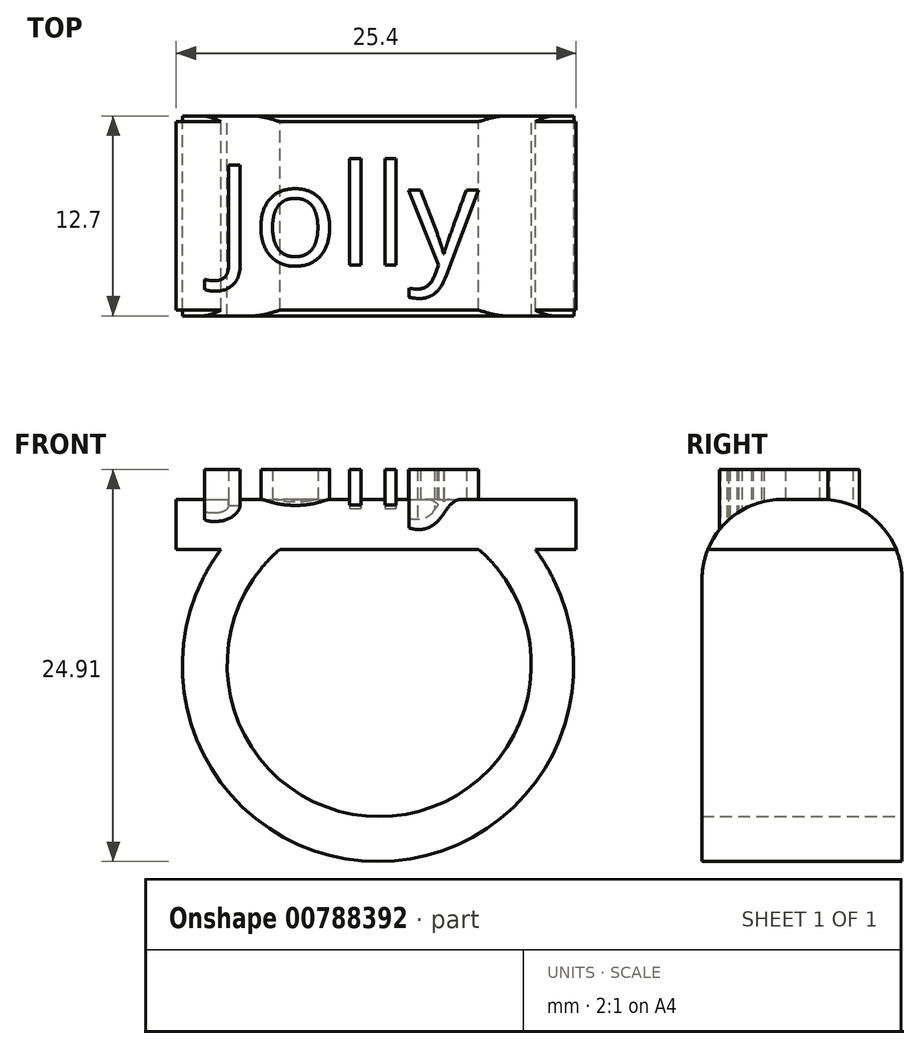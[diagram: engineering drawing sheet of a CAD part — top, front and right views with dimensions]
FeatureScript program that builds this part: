
annotation { "Feature Type Name" : "Feature", "Feature Type Description" : "" }
export const myFeature = defineFeature(function(context is Context, id is Id, definition is map)
    precondition{}
    {
        {
            var Q0;
            Q0=qCreatedBy(makeId("Top.planeOp"),FACE);
            var sketch = newSketch(context, id + "F0", { "sketchPlane" : qUnion([Q0])});
            skLineSegment(sketch, "E0.bottom", {"start": v(-13.4, 0) * mm, "end": v(12, 0) * mm});
            skLineSegment(sketch, "E0.top", {"start": v(-13.4, -12.7) * mm, "end": v(12, -12.7) * mm});
            skLineSegment(sketch, "E0.left", {"start": v(-13.4, 0) * mm, "end": v(-13.4, -12.7) * mm});
            skLineSegment(sketch, "E0.right", {"start": v(12, 0) * mm, "end": v(12, -12.7) * mm});
            skSolve(sketch);
        }
        {
            var Q0;
            Q0=qSketchRegion(id+"F0",true);
            extrude(context, id + "F1", {"entities" : qUnion([Q0]), "depth" : 3.17 * mm, "offsetDistance" : 25.4 * mm});
        }
        {
            var Q0;
            Q0=qCreatedBy(makeId("Front.planeOp"),FACE);
            var sketch = newSketch(context, id + "F2", { "sketchPlane" : qUnion([Q0])});
            skArc(sketch, "E1", {"start": v(-10.57, 0) * mm, "mid": v(-0.59, -19.83) * mm, "end": v(9.4, 0) * mm});
            skArc(sketch, "E2", {"start": v(-6.83, 0) * mm, "mid": v(-0.51, -16.97) * mm, "end": v(5.8, 0) * mm});
            skLineSegment(sketch, "E3", {"start": v(-10.57, 0) * mm, "end": v(-6.83, 0) * mm});
            skLineSegment(sketch, "E4", {"start": v(5.8, 0) * mm, "end": v(9.4, 0) * mm});
            skSolve(sketch);
        }
        {
            var Q0;
            Q0=qSketchRegion(id+"F2",true);
            extrude(context, id + "F3", {"entities" : qUnion([Q0]), "operationType" : NewBodyOperationType.ADD, "depth" : 12.7 * mm, "offsetDistance" : 25.4 * mm});
        }
        {
            var Q0;
            Q0=qCreatedBy(makeId("Top.planeOp"),FACE);
            var sketch = newSketch(context, id + "F4", { "sketchPlane" : qUnion([Q0])});
            skText(sketch, "E5", { "text": "Jolly ", "fontName": "OpenSans-Regular.ttf"});
            const initialGuessF4  = {"E5": [-0.0109, -0.00946, 1, 0, 0.00639]};
            skSetInitialGuess(sketch, initialGuessF4);
            skSolve(sketch);
        }
        {
            var Q0;
            Q0=makeQuery(id+"F1.opExtrude","CAP_EDGE",EDGE,{"disambiguationData":[OSD([sQuery(id+"F0.wireOp",EDGE,"E0.bottom")])],"isStart":false});
            var Q1;
            Q1=makeQuery(id+"F1.opExtrude","CAP_EDGE",EDGE,{"disambiguationData":[OSD([sQuery(id+"F0.wireOp",EDGE,"E0.top")])],"isStart":false});
            fillet(context, id + "F5", {"entities" : qUnion([Q0, Q1]), "radius" : 5.08 * mm, "tangentPropagation" : true, "allowEdgeOverflow" : false});
        }
        {
            var Q0;
            Q0 = qSketchRegion(id + "F4", true);
            extrude(context, id + "F6", {"entities" : qUnion([Q0]), "operationType" : NewBodyOperationType.ADD, "depth" : 5.08 * mm, "offsetDistance" : 25.4 * mm});
        }
    });
